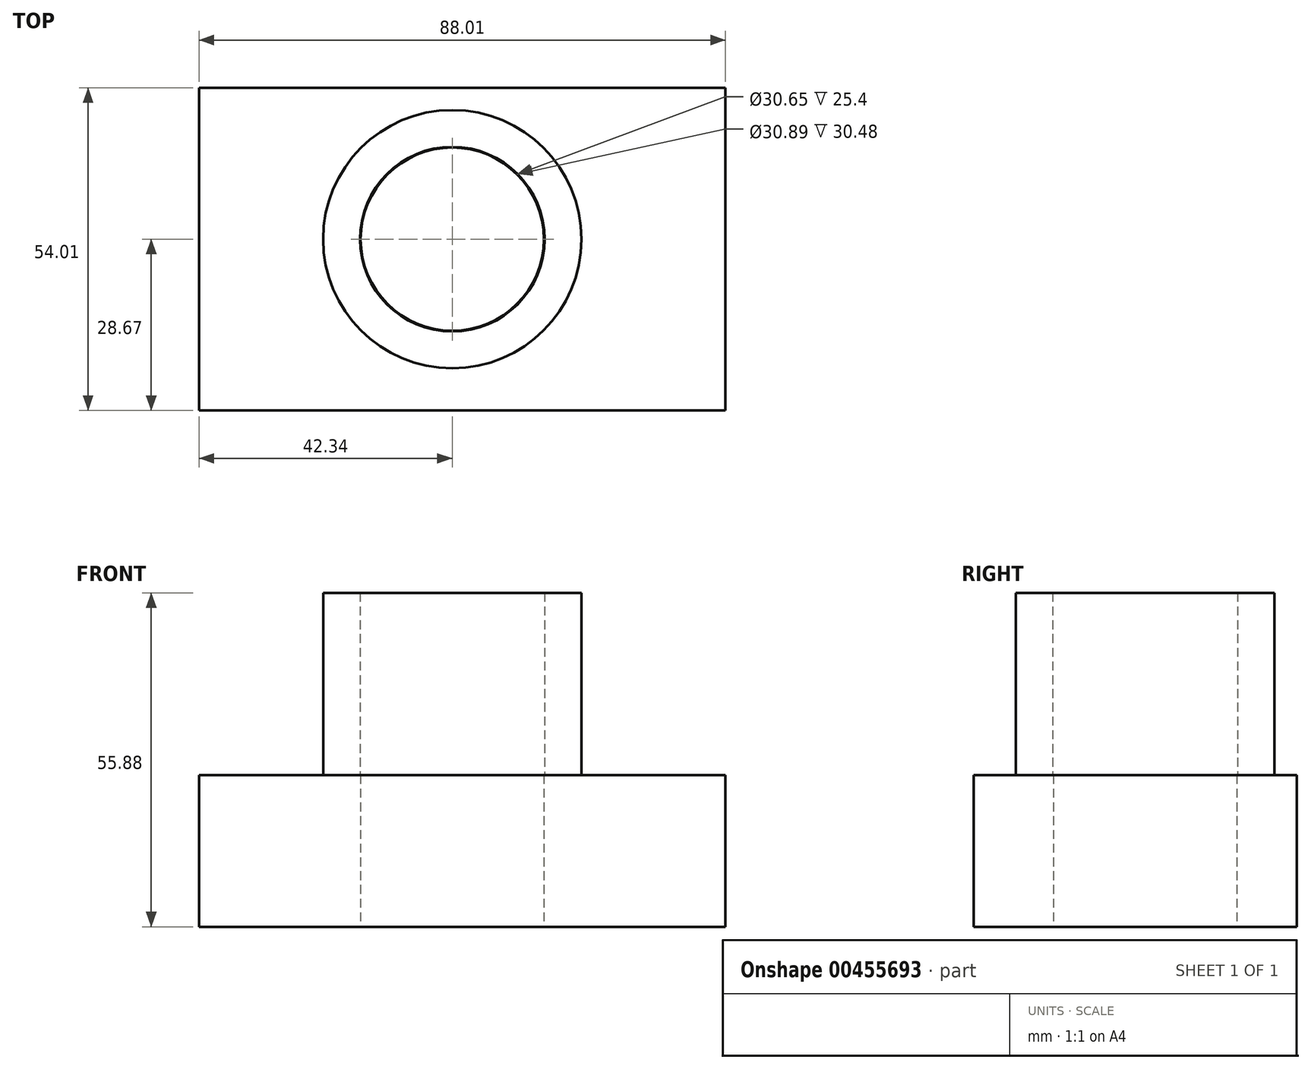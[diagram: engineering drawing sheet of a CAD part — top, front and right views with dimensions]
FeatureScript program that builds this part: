
annotation { "Feature Type Name" : "Feature", "Feature Type Description" : "" }
export const myFeature = defineFeature(function(context is Context, id is Id, definition is map)
    precondition{}
    {
        {
            var Q0;
            Q0=qCreatedBy(makeId("Top.planeOp"),FACE);
            var sketch = newSketch(context, id + "F0", { "sketchPlane" : qUnion([Q0])});
            skLineSegment(sketch, "E0.bottom", {"start": v(-42.34, 25.34) * mm, "end": v(45.67, 25.34) * mm});
            skLineSegment(sketch, "E0.top", {"start": v(-42.34, -28.67) * mm, "end": v(45.67, -28.67) * mm});
            skLineSegment(sketch, "E0.left", {"start": v(-42.34, 25.34) * mm, "end": v(-42.34, -28.67) * mm});
            skLineSegment(sketch, "E0.right", {"start": v(45.67, 25.34) * mm, "end": v(45.67, -28.67) * mm});
            skCircle(sketch, "E1", {"center": v(0, 0) * mm, "radius": 15.32 * mm});
            skSolve(sketch);
        }
        {
            var Q0;
            Q0=makeQuery(id+"F0.imprint","IMPRINT",FACE,{"disambiguationData":[TD([[makeQuery(id+"F0.imprint","IMPRINT",EDGE,{"derivedFrom":sQuery(id+"F0.wireOp",EDGE,"E0.bottom")}),-1.0]])]});
            extrude(context, id + "F1", {"entities" : qUnion([Q0]), "depth" : 25.4 * mm});
        }
        {
            var Q0;
            Q0=qCreatedBy(makeId("Top.planeOp"),FACE);
            var sketch = newSketch(context, id + "F2", { "sketchPlane" : qUnion([Q0])});
            skCircle(sketch, "E2", {"center": v(0, 0) * mm, "radius": 15.44 * mm});
            skCircle(sketch, "E3", {"center": v(0, 0) * mm, "radius": 21.6 * mm});
            skSolve(sketch);
        }
        {
            var Q0;
            Q0 = qSketchRegion(id + "F2", true);
            extrude(context, id + "F3", {"entities" : qUnion([Q0]), "operationType" : NewBodyOperationType.ADD, "depth" : 55.88 * mm});
        }
    });
